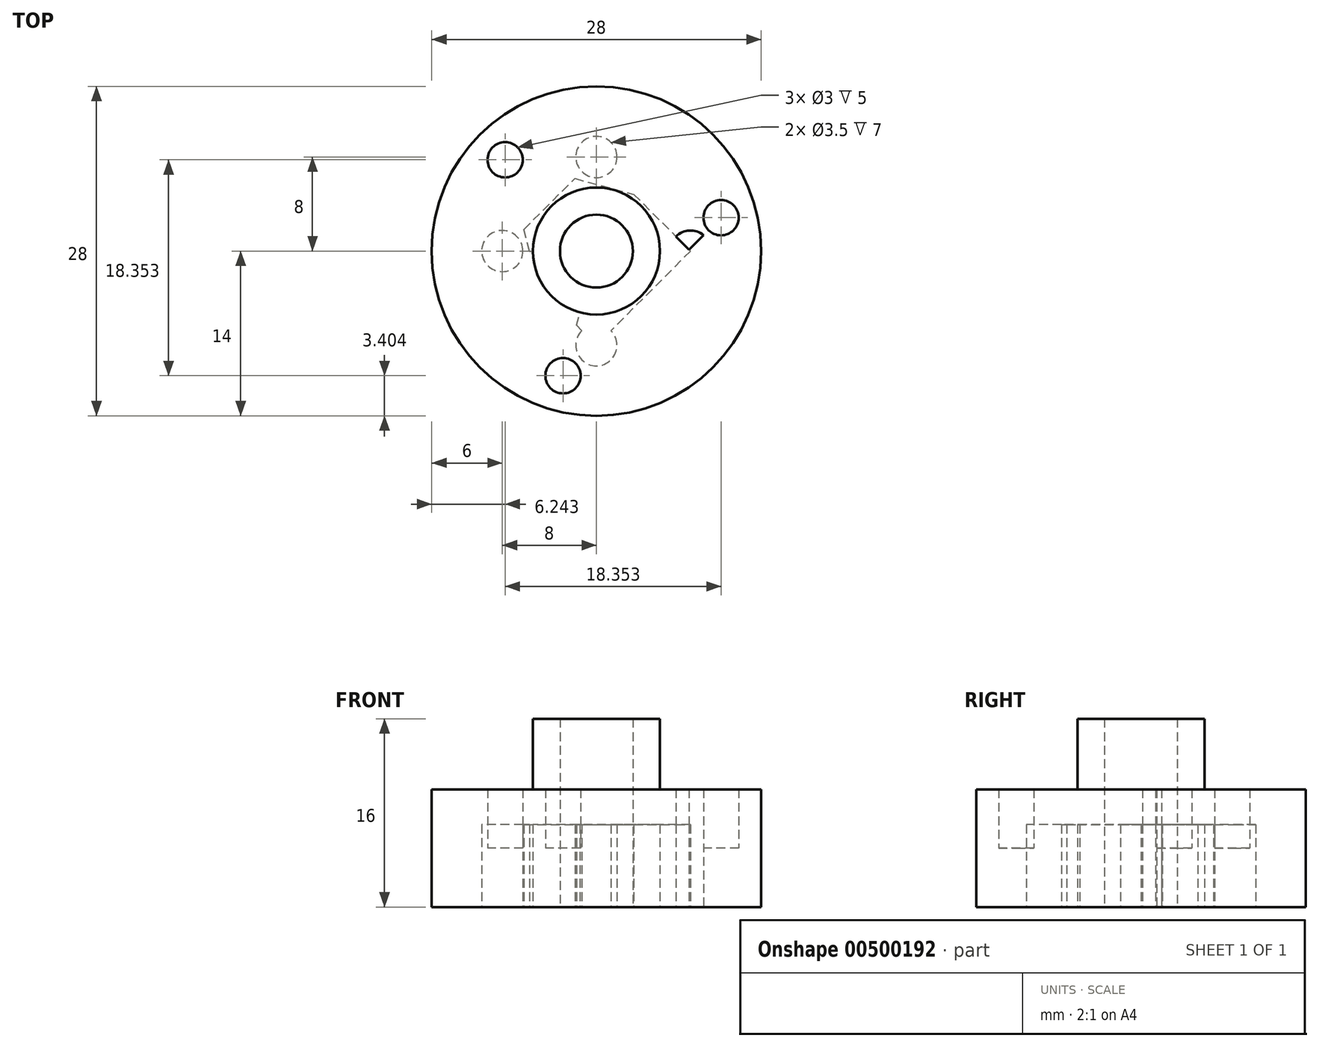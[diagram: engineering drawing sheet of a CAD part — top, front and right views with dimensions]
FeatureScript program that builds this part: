
annotation { "Feature Type Name" : "Feature", "Feature Type Description" : "" }
export const myFeature = defineFeature(function(context is Context, id is Id, definition is map)
    precondition{}
    {
        {
            var Q0;
            Q0=qCreatedBy(makeId("Top.planeOp"),FACE);
            var sketch = newSketch(context, id + "F0", { "sketchPlane" : qUnion([Q0])});
            skCircle(sketch, "E0", {"center": v(0, 0) * mm, "radius": 14 * mm});
            skCircle(sketch, "E1", {"center": v(0, 0) * mm, "radius": 3.1 * mm});
            skCircle(sketch, "E2", {"center": v(0, 0) * mm, "radius": 5.4 * mm});
            skLineSegment(sketch, "E3.0", {"start": v(-2.84, -10.6) * mm, "end": v(-7.76, 7.76) * mm});
            skLineSegment(sketch, "E3.1", {"start": v(-7.76, 7.76) * mm, "end": v(10.6, 2.84) * mm});
            skLineSegment(sketch, "E3.2", {"start": v(10.6, 2.84) * mm, "end": v(-2.84, -10.6) * mm});
            skLineSegment(sketch, "E4.0", {"start": v(8, 0) * mm, "end": v(0, -8) * mm});
            skLineSegment(sketch, "E4.1", {"start": v(0, -8) * mm, "end": v(-8, 0) * mm});
            skLineSegment(sketch, "E4.2", {"start": v(-8, 0) * mm, "end": v(0, 8) * mm});
            skLineSegment(sketch, "E4.3", {"start": v(0, 8) * mm, "end": v(8, 0) * mm});
            skPoint(sketch, "E5", {"position": v(-2.84, -10.6) * mm});
            skPoint(sketch, "E6", {"position": v(0, -8) * mm});
            skCircle(sketch, "E7", {"center": v(-8, 0) * mm, "radius": 1.75 * mm});
            skCircle(sketch, "E8", {"center": v(0, 8) * mm, "radius": 1.75 * mm});
            skCircle(sketch, "E9", {"center": v(8, 0) * mm, "radius": 1.75 * mm});
            skCircle(sketch, "E10", {"center": v(0, -8) * mm, "radius": 1.75 * mm});
            skLineSegment(sketch, "E11", {"start": v(-8, 0) * mm, "end": v(0, 0) * mm});
            skLineSegment(sketch, "E12", {"start": v(-2.84, -10.6) * mm, "end": v(0, 0) * mm});
            skCircle(sketch, "E13", {"center": v(-7.76, 7.76) * mm, "radius": 1.5 * mm});
            skCircle(sketch, "E14", {"center": v(-2.84, -10.6) * mm, "radius": 1.5 * mm});
            skCircle(sketch, "E15", {"center": v(10.6, 2.84) * mm, "radius": 1.5 * mm});
            skSolve(sketch);
        }
        {
            var Q0;
            Q0=makeQuery(id+"F0.imprint","IMPRINT",FACE,{"disambiguationData":[TD([[makeQuery(id+"F0.imprint","IMPRINT",EDGE,{"derivedFrom":sQuery(id+"F0.wireOp",EDGE,"E0")}),1.0]])]});
            var Q1;
            {var subQ5=sQuery(id+"F0.wireOp",EDGE,"E11");var subQ14=sQuery(id+"F0.wireOp",EDGE,"E2");var subQ15=makeQuery(id+"F0.imprint","INTERSECT",VERTEX,{"derivedFrom":[subQ14,subQ5]});Q1=makeQuery(id+"F0.imprint","IMPRINT",FACE,{"disambiguationData":[TD([[makeQuery(id+"F0.imprint","IMPRINT",EDGE,{"disambiguationData":[TD([[subQ15,1.0]])],"derivedFrom":subQ14}),-1.0]])]});}
            var Q2;
            {var subQ0=sQuery(id+"F0.wireOp",EDGE,"E9");var subQ1=sQuery(id+"F0.wireOp",EDGE,"E3.2");var subQ2=makeQuery(id+"F0.imprint","INTERSECT",VERTEX,{"disambiguationData":[OD(1.0)],"derivedFrom":[subQ1,subQ0]});Q2=makeQuery(id+"F0.imprint","IMPRINT",FACE,{"disambiguationData":[TD([[makeQuery(id+"F0.imprint","IMPRINT",EDGE,{"disambiguationData":[TD([[subQ2,-1.0]])],"derivedFrom":subQ1}),1.0]])]});}
            var Q3;
            {var subQ0=sQuery(id+"F0.wireOp",EDGE,"E4.3");var subQ1=sQuery(id+"F0.wireOp",EDGE,"E3.1");var subQ2=makeQuery(id+"F0.imprint","INTERSECT",VERTEX,{"derivedFrom":[subQ1,subQ0]});Q3=makeQuery(id+"F0.imprint","IMPRINT",FACE,{"disambiguationData":[TD([[makeQuery(id+"F0.imprint","IMPRINT",EDGE,{"disambiguationData":[TD([[subQ2,-1.0]])],"derivedFrom":subQ1}),-1.0]])]});}
            var Q4;
            {var subQ0=sQuery(id+"F0.wireOp",EDGE,"E4.2");var subQ1=sQuery(id+"F0.wireOp",EDGE,"E3.1");var subQ2=makeQuery(id+"F0.imprint","INTERSECT",VERTEX,{"derivedFrom":[subQ1,subQ0]});Q4=makeQuery(id+"F0.imprint","IMPRINT",FACE,{"disambiguationData":[TD([[makeQuery(id+"F0.imprint","IMPRINT",EDGE,{"disambiguationData":[TD([[subQ2,-1.0]])],"derivedFrom":subQ1}),1.0]])]});}
            var Q5;
            {var subQ0=sQuery(id+"F0.wireOp",EDGE,"E4.2");var subQ1=sQuery(id+"F0.wireOp",EDGE,"E3.0");var subQ2=makeQuery(id+"F0.imprint","INTERSECT",VERTEX,{"derivedFrom":[subQ1,subQ0]});Q5=makeQuery(id+"F0.imprint","IMPRINT",FACE,{"disambiguationData":[TD([[makeQuery(id+"F0.imprint","IMPRINT",EDGE,{"disambiguationData":[TD([[subQ2,-1.0]])],"derivedFrom":subQ1}),-1.0]])]});}
            var Q6;
            {var subQ0=sQuery(id+"F0.wireOp",EDGE,"E4.1");var subQ1=sQuery(id+"F0.wireOp",EDGE,"E3.0");var subQ2=makeQuery(id+"F0.imprint","INTERSECT",VERTEX,{"derivedFrom":[subQ1,subQ0]});Q6=makeQuery(id+"F0.imprint","IMPRINT",FACE,{"disambiguationData":[TD([[makeQuery(id+"F0.imprint","IMPRINT",EDGE,{"disambiguationData":[TD([[subQ2,-1.0]])],"derivedFrom":subQ1}),1.0]])]});}
            var Q7;
            {var subQ0=sQuery(id+"F0.wireOp",EDGE,"E11");var subQ1=sQuery(id+"F0.wireOp",EDGE,"E3.0");var subQ2=makeQuery(id+"F0.imprint","INTERSECT",VERTEX,{"derivedFrom":[subQ1,subQ0]});Q7=makeQuery(id+"F0.imprint","IMPRINT",FACE,{"disambiguationData":[TD([[makeQuery(id+"F0.imprint","IMPRINT",EDGE,{"disambiguationData":[TD([[subQ2,-1.0]])],"derivedFrom":subQ1}),1.0]])]});}
            var Q8;
            {var subQ0=sQuery(id+"F0.wireOp",EDGE,"E14");var subQ1=sQuery(id+"F0.wireOp",EDGE,"E3.0");var subQ2=makeQuery(id+"F0.imprint","INTERSECT",VERTEX,{"derivedFrom":[subQ1,subQ0]});Q8=makeQuery(id+"F0.imprint","IMPRINT",FACE,{"disambiguationData":[TD([[makeQuery(id+"F0.imprint","IMPRINT",EDGE,{"disambiguationData":[TD([[subQ2,-1.0]])],"derivedFrom":subQ1}),-1.0]])]});}
            var Q9;
            {var subQ0=sQuery(id+"F0.wireOp",EDGE,"E10");var subQ1=sQuery(id+"F0.wireOp",EDGE,"E3.2");var subQ2=makeQuery(id+"F0.imprint","INTERSECT",VERTEX,{"disambiguationData":[OD(1.0)],"derivedFrom":[subQ1,subQ0]});Q9=makeQuery(id+"F0.imprint","IMPRINT",FACE,{"disambiguationData":[TD([[makeQuery(id+"F0.imprint","IMPRINT",EDGE,{"disambiguationData":[TD([[subQ2,-1.0]])],"derivedFrom":subQ1}),-1.0]])]});}
            var Q10;
            {var subQ0=sQuery(id+"F0.wireOp",EDGE,"E11");var subQ1=sQuery(id+"F0.wireOp",EDGE,"E2");var subQ2=makeQuery(id+"F0.imprint","INTERSECT",VERTEX,{"derivedFrom":[subQ1,subQ0]});Q10=makeQuery(id+"F0.imprint","IMPRINT",FACE,{"disambiguationData":[TD([[makeQuery(id+"F0.imprint","IMPRINT",EDGE,{"disambiguationData":[TD([[subQ2,-1.0]])],"derivedFrom":subQ1}),-1.0]])]});}
            var Q11;
            {var subQ1=sQuery(id+"F0.wireOp",EDGE,"E4.2");var subQ3=sQuery(id+"F0.wireOp",EDGE,"E7");var subQ4=makeQuery(id+"F0.imprint","INTERSECT",VERTEX,{"derivedFrom":[subQ1,subQ3]});Q11=makeQuery(id+"F0.imprint","IMPRINT",FACE,{"disambiguationData":[TD([[makeQuery(id+"F0.imprint","IMPRINT",EDGE,{"disambiguationData":[TD([[subQ4,1.0]])],"derivedFrom":subQ3}),1.0]])]});}
            var Q12;
            {var subQ1=sQuery(id+"F0.wireOp",EDGE,"E4.1");var subQ3=sQuery(id+"F0.wireOp",EDGE,"E7");var subQ4=makeQuery(id+"F0.imprint","INTERSECT",VERTEX,{"derivedFrom":[subQ1,subQ3]});Q12=makeQuery(id+"F0.imprint","IMPRINT",FACE,{"disambiguationData":[TD([[makeQuery(id+"F0.imprint","IMPRINT",EDGE,{"disambiguationData":[TD([[subQ4,-1.0]])],"derivedFrom":subQ3}),1.0]])]});}
            var Q13;
            {var subQ1=sQuery(id+"F0.wireOp",EDGE,"E4.1");var subQ3=sQuery(id+"F0.wireOp",EDGE,"E7");var subQ4=makeQuery(id+"F0.imprint","INTERSECT",VERTEX,{"derivedFrom":[subQ1,subQ3]});Q13=makeQuery(id+"F0.imprint","IMPRINT",FACE,{"disambiguationData":[TD([[makeQuery(id+"F0.imprint","IMPRINT",EDGE,{"disambiguationData":[TD([[subQ4,1.0]])],"derivedFrom":subQ3}),1.0]])]});}
            var Q14;
            {var subQ0=sQuery(id+"F0.wireOp",EDGE,"E4.3");var subQ1=sQuery(id+"F0.wireOp",EDGE,"E4.2");var subQ2=makeQuery(id+"F0.imprint","INTERSECT",VERTEX,{"derivedFrom":[subQ1,subQ0]});Q14=makeQuery(id+"F0.imprint","IMPRINT",FACE,{"disambiguationData":[TD([[makeQuery(id+"F0.imprint","IMPRINT",EDGE,{"disambiguationData":[TD([[subQ2,1.0]])],"derivedFrom":subQ1}),1.0]])]});}
            var Q15;
            {var subQ0=sQuery(id+"F0.wireOp",EDGE,"E4.3");var subQ1=sQuery(id+"F0.wireOp",EDGE,"E4.2");var subQ2=makeQuery(id+"F0.imprint","INTERSECT",VERTEX,{"derivedFrom":[subQ1,subQ0]});Q15=makeQuery(id+"F0.imprint","IMPRINT",FACE,{"disambiguationData":[TD([[makeQuery(id+"F0.imprint","IMPRINT",EDGE,{"disambiguationData":[TD([[subQ2,1.0]])],"derivedFrom":subQ1}),-1.0]])]});}
            var Q16;
            {var subQ0=sQuery(id+"F0.wireOp",EDGE,"E9");var subQ1=sQuery(id+"F0.wireOp",EDGE,"E3.2");var subQ2=makeQuery(id+"F0.imprint","INTERSECT",VERTEX,{"disambiguationData":[OD(0.0)],"derivedFrom":[subQ1,subQ0]});Q16=makeQuery(id+"F0.imprint","IMPRINT",FACE,{"disambiguationData":[TD([[makeQuery(id+"F0.imprint","IMPRINT",EDGE,{"disambiguationData":[TD([[subQ2,-1.0]])],"derivedFrom":subQ1}),1.0]])]});}
            var Q17;
            {var subQ0=sQuery(id+"F0.wireOp",EDGE,"E4.3");var subQ1=sQuery(id+"F0.wireOp",EDGE,"E3.2");var subQ2=makeQuery(id+"F0.imprint","INTERSECT",VERTEX,{"derivedFrom":[subQ1,subQ0]});Q17=makeQuery(id+"F0.imprint","IMPRINT",FACE,{"disambiguationData":[TD([[makeQuery(id+"F0.imprint","IMPRINT",EDGE,{"disambiguationData":[TD([[subQ2,-1.0]])],"derivedFrom":subQ1}),-1.0]])]});}
            var Q18;
            {var subQ0=sQuery(id+"F0.wireOp",EDGE,"E4.1");var subQ1=sQuery(id+"F0.wireOp",EDGE,"E3.2");var subQ2=makeQuery(id+"F0.imprint","INTERSECT",VERTEX,{"derivedFrom":[subQ1,subQ0]});Q18=makeQuery(id+"F0.imprint","IMPRINT",FACE,{"disambiguationData":[TD([[makeQuery(id+"F0.imprint","IMPRINT",EDGE,{"disambiguationData":[TD([[subQ2,-1.0]])],"derivedFrom":subQ1}),1.0]])]});}
            var Q19;
            {var subQ0=sQuery(id+"F0.wireOp",EDGE,"E10");var subQ1=sQuery(id+"F0.wireOp",EDGE,"E3.2");var subQ2=makeQuery(id+"F0.imprint","INTERSECT",VERTEX,{"disambiguationData":[OD(0.0)],"derivedFrom":[subQ1,subQ0]});Q19=makeQuery(id+"F0.imprint","IMPRINT",FACE,{"disambiguationData":[TD([[makeQuery(id+"F0.imprint","IMPRINT",EDGE,{"disambiguationData":[TD([[subQ2,-1.0]])],"derivedFrom":subQ1}),-1.0]])]});}
            var Q20;
            {var subQ0=sQuery(id+"F0.wireOp",EDGE,"E4.1");var subQ1=sQuery(id+"F0.wireOp",EDGE,"E3.2");var subQ2=makeQuery(id+"F0.imprint","INTERSECT",VERTEX,{"derivedFrom":[subQ1,subQ0]});Q20=makeQuery(id+"F0.imprint","IMPRINT",FACE,{"disambiguationData":[TD([[makeQuery(id+"F0.imprint","IMPRINT",EDGE,{"disambiguationData":[TD([[subQ2,-1.0]])],"derivedFrom":subQ1}),-1.0]])]});}
            var Q21;
            {var subQ0=sQuery(id+"F0.wireOp",EDGE,"E10");var subQ1=sQuery(id+"F0.wireOp",EDGE,"E3.2");var subQ2=makeQuery(id+"F0.imprint","INTERSECT",VERTEX,{"disambiguationData":[OD(0.0)],"derivedFrom":[subQ1,subQ0]});Q21=makeQuery(id+"F0.imprint","IMPRINT",FACE,{"disambiguationData":[TD([[makeQuery(id+"F0.imprint","IMPRINT",EDGE,{"disambiguationData":[TD([[subQ2,-1.0]])],"derivedFrom":subQ1}),1.0]])]});}
            var Q22;
            {var subQ0=sQuery(id+"F0.wireOp",EDGE,"E9");var subQ1=sQuery(id+"F0.wireOp",EDGE,"E3.2");var subQ2=makeQuery(id+"F0.imprint","INTERSECT",VERTEX,{"disambiguationData":[OD(0.0)],"derivedFrom":[subQ1,subQ0]});Q22=makeQuery(id+"F0.imprint","IMPRINT",FACE,{"disambiguationData":[TD([[makeQuery(id+"F0.imprint","IMPRINT",EDGE,{"disambiguationData":[TD([[subQ2,-1.0]])],"derivedFrom":subQ1}),-1.0]])]});}
            var Q23;
            {var subQ0=sQuery(id+"F0.wireOp",EDGE,"E4.3");var subQ1=sQuery(id+"F0.wireOp",EDGE,"E3.2");var subQ2=makeQuery(id+"F0.imprint","INTERSECT",VERTEX,{"derivedFrom":[subQ1,subQ0]});Q23=makeQuery(id+"F0.imprint","IMPRINT",FACE,{"disambiguationData":[TD([[makeQuery(id+"F0.imprint","IMPRINT",EDGE,{"disambiguationData":[TD([[subQ2,-1.0]])],"derivedFrom":subQ1}),1.0]])]});}
            extrude(context, id + "F1", {"entities" : qUnion([Q0, Q1, Q2, Q3, Q4, Q5, Q6, Q7, Q8, Q9, Q10, Q11, Q12, Q13, Q14, Q15, Q16, Q17, Q18, Q19, Q20, Q21, Q22, Q23]), "depth" : 10 * mm});
        }
        {
            var Q0;
            {var subQ0=sQuery(id+"F0.wireOp",EDGE,"E11");var subQ1=sQuery(id+"F0.wireOp",EDGE,"E1");var subQ2=makeQuery(id+"F0.imprint","INTERSECT",VERTEX,{"derivedFrom":[subQ1,subQ0]});Q0=makeQuery(id+"F0.imprint","IMPRINT",FACE,{"disambiguationData":[TD([[makeQuery(id+"F0.imprint","IMPRINT",EDGE,{"disambiguationData":[TD([[subQ2,-1.0]])],"derivedFrom":subQ1}),-1.0]])]});}
            var Q1;
            {var subQ0=sQuery(id+"F0.wireOp",EDGE,"E11");var subQ1=sQuery(id+"F0.wireOp",EDGE,"E1");var subQ2=makeQuery(id+"F0.imprint","INTERSECT",VERTEX,{"derivedFrom":[subQ1,subQ0]});Q1=makeQuery(id+"F0.imprint","IMPRINT",FACE,{"disambiguationData":[TD([[makeQuery(id+"F0.imprint","IMPRINT",EDGE,{"disambiguationData":[TD([[subQ2,1.0]])],"derivedFrom":subQ1}),-1.0]])]});}
            extrude(context, id + "F2", {"entities" : qUnion([Q0, Q1]), "operationType" : NewBodyOperationType.ADD, "depth" : 16 * mm});
        }
        {
            var Q0;
            {var subQ1=sQuery(id+"F0.wireOp",EDGE,"E3.2");var subQ3=sQuery(id+"F0.wireOp",EDGE,"E14");var subQ4=makeQuery(id+"F0.imprint","INTERSECT",VERTEX,{"derivedFrom":[subQ1,subQ3]});Q0=makeQuery(id+"F0.imprint","IMPRINT",FACE,{"disambiguationData":[TD([[makeQuery(id+"F0.imprint","IMPRINT",EDGE,{"disambiguationData":[TD([[subQ4,-1.0]])],"derivedFrom":subQ3}),1.0]])]});}
            var Q1;
            {var subQ1=sQuery(id+"F0.wireOp",EDGE,"E3.0");var subQ3=sQuery(id+"F0.wireOp",EDGE,"E14");var subQ4=makeQuery(id+"F0.imprint","INTERSECT",VERTEX,{"derivedFrom":[subQ1,subQ3]});Q1=makeQuery(id+"F0.imprint","IMPRINT",FACE,{"disambiguationData":[TD([[makeQuery(id+"F0.imprint","IMPRINT",EDGE,{"disambiguationData":[TD([[subQ4,1.0]])],"derivedFrom":subQ3}),1.0]])]});}
            var Q2;
            {var subQ1=sQuery(id+"F0.wireOp",EDGE,"E3.0");var subQ3=sQuery(id+"F0.wireOp",EDGE,"E14");var subQ4=makeQuery(id+"F0.imprint","INTERSECT",VERTEX,{"derivedFrom":[subQ1,subQ3]});Q2=makeQuery(id+"F0.imprint","IMPRINT",FACE,{"disambiguationData":[TD([[makeQuery(id+"F0.imprint","IMPRINT",EDGE,{"disambiguationData":[TD([[subQ4,-1.0]])],"derivedFrom":subQ3}),1.0]])]});}
            var Q3;
            {var subQ0=sQuery(id+"F0.wireOp",EDGE,"E3.2");var subQ1=sQuery(id+"F0.wireOp",EDGE,"E3.1");var subQ2=makeQuery(id+"F0.imprint","INTERSECT",VERTEX,{"derivedFrom":[subQ1,subQ0]});Q3=makeQuery(id+"F0.imprint","IMPRINT",FACE,{"disambiguationData":[TD([[makeQuery(id+"F0.imprint","IMPRINT",EDGE,{"disambiguationData":[TD([[subQ2,1.0]])],"derivedFrom":subQ1}),-1.0]])]});}
            var Q4;
            {var subQ0=sQuery(id+"F0.wireOp",EDGE,"E3.2");var subQ1=sQuery(id+"F0.wireOp",EDGE,"E3.1");var subQ2=makeQuery(id+"F0.imprint","INTERSECT",VERTEX,{"derivedFrom":[subQ1,subQ0]});Q4=makeQuery(id+"F0.imprint","IMPRINT",FACE,{"disambiguationData":[TD([[makeQuery(id+"F0.imprint","IMPRINT",EDGE,{"disambiguationData":[TD([[subQ2,1.0]])],"derivedFrom":subQ1}),1.0]])]});}
            var Q5;
            {var subQ0=sQuery(id+"F0.wireOp",EDGE,"E3.1");var subQ1=sQuery(id+"F0.wireOp",EDGE,"E3.0");var subQ2=makeQuery(id+"F0.imprint","INTERSECT",VERTEX,{"derivedFrom":[subQ1,subQ0]});Q5=makeQuery(id+"F0.imprint","IMPRINT",FACE,{"disambiguationData":[TD([[makeQuery(id+"F0.imprint","IMPRINT",EDGE,{"disambiguationData":[TD([[subQ2,1.0]])],"derivedFrom":subQ1}),1.0]])]});}
            var Q6;
            {var subQ0=sQuery(id+"F0.wireOp",EDGE,"E3.1");var subQ1=sQuery(id+"F0.wireOp",EDGE,"E3.0");var subQ2=makeQuery(id+"F0.imprint","INTERSECT",VERTEX,{"derivedFrom":[subQ1,subQ0]});Q6=makeQuery(id+"F0.imprint","IMPRINT",FACE,{"disambiguationData":[TD([[makeQuery(id+"F0.imprint","IMPRINT",EDGE,{"disambiguationData":[TD([[subQ2,1.0]])],"derivedFrom":subQ1}),-1.0]])]});}
            extrude(context, id + "F3", {"entities" : qUnion([Q0, Q1, Q2, Q3, Q4, Q5, Q6]), "operationType" : NewBodyOperationType.ADD, "depth" : 5 * mm});
        }
        {
            var Q0;
            {var subQ0=sQuery(id+"F0.wireOp",EDGE,"E4.3");var subQ1=sQuery(id+"F0.wireOp",EDGE,"E4.2");var subQ2=makeQuery(id+"F0.imprint","INTERSECT",VERTEX,{"derivedFrom":[subQ1,subQ0]});Q0=makeQuery(id+"F0.imprint","IMPRINT",FACE,{"disambiguationData":[TD([[makeQuery(id+"F0.imprint","IMPRINT",EDGE,{"disambiguationData":[TD([[subQ2,1.0]])],"derivedFrom":subQ1}),1.0]])]});}
            var Q1;
            {var subQ0=sQuery(id+"F0.wireOp",EDGE,"E4.3");var subQ1=sQuery(id+"F0.wireOp",EDGE,"E4.2");var subQ2=makeQuery(id+"F0.imprint","INTERSECT",VERTEX,{"derivedFrom":[subQ1,subQ0]});Q1=makeQuery(id+"F0.imprint","IMPRINT",FACE,{"disambiguationData":[TD([[makeQuery(id+"F0.imprint","IMPRINT",EDGE,{"disambiguationData":[TD([[subQ2,1.0]])],"derivedFrom":subQ1}),-1.0]])]});}
            var Q2;
            {var subQ1=sQuery(id+"F0.wireOp",EDGE,"E4.1");var subQ3=sQuery(id+"F0.wireOp",EDGE,"E7");var subQ4=makeQuery(id+"F0.imprint","INTERSECT",VERTEX,{"derivedFrom":[subQ1,subQ3]});Q2=makeQuery(id+"F0.imprint","IMPRINT",FACE,{"disambiguationData":[TD([[makeQuery(id+"F0.imprint","IMPRINT",EDGE,{"disambiguationData":[TD([[subQ4,1.0]])],"derivedFrom":subQ3}),1.0]])]});}
            var Q3;
            {var subQ1=sQuery(id+"F0.wireOp",EDGE,"E4.1");var subQ3=sQuery(id+"F0.wireOp",EDGE,"E7");var subQ4=makeQuery(id+"F0.imprint","INTERSECT",VERTEX,{"derivedFrom":[subQ1,subQ3]});Q3=makeQuery(id+"F0.imprint","IMPRINT",FACE,{"disambiguationData":[TD([[makeQuery(id+"F0.imprint","IMPRINT",EDGE,{"disambiguationData":[TD([[subQ4,-1.0]])],"derivedFrom":subQ3}),1.0]])]});}
            var Q4;
            {var subQ1=sQuery(id+"F0.wireOp",EDGE,"E4.2");var subQ3=sQuery(id+"F0.wireOp",EDGE,"E7");var subQ4=makeQuery(id+"F0.imprint","INTERSECT",VERTEX,{"derivedFrom":[subQ1,subQ3]});Q4=makeQuery(id+"F0.imprint","IMPRINT",FACE,{"disambiguationData":[TD([[makeQuery(id+"F0.imprint","IMPRINT",EDGE,{"disambiguationData":[TD([[subQ4,1.0]])],"derivedFrom":subQ3}),1.0]])]});}
            var Q5;
            {var subQ0=sQuery(id+"F0.wireOp",EDGE,"E10");var subQ1=sQuery(id+"F0.wireOp",EDGE,"E3.2");var subQ2=makeQuery(id+"F0.imprint","INTERSECT",VERTEX,{"disambiguationData":[OD(0.0)],"derivedFrom":[subQ1,subQ0]});Q5=makeQuery(id+"F0.imprint","IMPRINT",FACE,{"disambiguationData":[TD([[makeQuery(id+"F0.imprint","IMPRINT",EDGE,{"disambiguationData":[TD([[subQ2,-1.0]])],"derivedFrom":subQ1}),-1.0]])]});}
            var Q6;
            {var subQ0=sQuery(id+"F0.wireOp",EDGE,"E4.1");var subQ1=sQuery(id+"F0.wireOp",EDGE,"E3.2");var subQ2=makeQuery(id+"F0.imprint","INTERSECT",VERTEX,{"derivedFrom":[subQ1,subQ0]});Q6=makeQuery(id+"F0.imprint","IMPRINT",FACE,{"disambiguationData":[TD([[makeQuery(id+"F0.imprint","IMPRINT",EDGE,{"disambiguationData":[TD([[subQ2,-1.0]])],"derivedFrom":subQ1}),-1.0]])]});}
            var Q7;
            {var subQ0=sQuery(id+"F0.wireOp",EDGE,"E10");var subQ1=sQuery(id+"F0.wireOp",EDGE,"E3.2");var subQ2=makeQuery(id+"F0.imprint","INTERSECT",VERTEX,{"disambiguationData":[OD(0.0)],"derivedFrom":[subQ1,subQ0]});Q7=makeQuery(id+"F0.imprint","IMPRINT",FACE,{"disambiguationData":[TD([[makeQuery(id+"F0.imprint","IMPRINT",EDGE,{"disambiguationData":[TD([[subQ2,-1.0]])],"derivedFrom":subQ1}),1.0]])]});}
            var Q8;
            {var subQ0=sQuery(id+"F0.wireOp",EDGE,"E4.1");var subQ1=sQuery(id+"F0.wireOp",EDGE,"E3.2");var subQ2=makeQuery(id+"F0.imprint","INTERSECT",VERTEX,{"derivedFrom":[subQ1,subQ0]});Q8=makeQuery(id+"F0.imprint","IMPRINT",FACE,{"disambiguationData":[TD([[makeQuery(id+"F0.imprint","IMPRINT",EDGE,{"disambiguationData":[TD([[subQ2,-1.0]])],"derivedFrom":subQ1}),1.0]])]});}
            var Q9;
            {var subQ0=sQuery(id+"F0.wireOp",EDGE,"E9");var subQ1=sQuery(id+"F0.wireOp",EDGE,"E3.2");var subQ2=makeQuery(id+"F0.imprint","INTERSECT",VERTEX,{"disambiguationData":[OD(0.0)],"derivedFrom":[subQ1,subQ0]});Q9=makeQuery(id+"F0.imprint","IMPRINT",FACE,{"disambiguationData":[TD([[makeQuery(id+"F0.imprint","IMPRINT",EDGE,{"disambiguationData":[TD([[subQ2,-1.0]])],"derivedFrom":subQ1}),-1.0]])]});}
            var Q10;
            {var subQ0=sQuery(id+"F0.wireOp",EDGE,"E4.3");var subQ1=sQuery(id+"F0.wireOp",EDGE,"E3.2");var subQ2=makeQuery(id+"F0.imprint","INTERSECT",VERTEX,{"derivedFrom":[subQ1,subQ0]});Q10=makeQuery(id+"F0.imprint","IMPRINT",FACE,{"disambiguationData":[TD([[makeQuery(id+"F0.imprint","IMPRINT",EDGE,{"disambiguationData":[TD([[subQ2,-1.0]])],"derivedFrom":subQ1}),-1.0]])]});}
            var Q11;
            {var subQ0=sQuery(id+"F0.wireOp",EDGE,"E9");var subQ1=sQuery(id+"F0.wireOp",EDGE,"E3.2");var subQ2=makeQuery(id+"F0.imprint","INTERSECT",VERTEX,{"disambiguationData":[OD(0.0)],"derivedFrom":[subQ1,subQ0]});Q11=makeQuery(id+"F0.imprint","IMPRINT",FACE,{"disambiguationData":[TD([[makeQuery(id+"F0.imprint","IMPRINT",EDGE,{"disambiguationData":[TD([[subQ2,-1.0]])],"derivedFrom":subQ1}),1.0]])]});}
            var Q12;
            {var subQ0=sQuery(id+"F0.wireOp",EDGE,"E9");var subQ1=sQuery(id+"F0.wireOp",EDGE,"E3.2");var subQ2=makeQuery(id+"F0.imprint","INTERSECT",VERTEX,{"disambiguationData":[OD(0.0)],"derivedFrom":[subQ1,subQ0]});Q12=makeQuery(id+"F0.imprint","IMPRINT",FACE,{"disambiguationData":[TD([[makeQuery(id+"F0.imprint","IMPRINT",EDGE,{"disambiguationData":[TD([[subQ2,-1.0]])],"derivedFrom":subQ1}),1.0]])]});}
            var Q13;
            {var subQ0=sQuery(id+"F0.wireOp",EDGE,"E4.3");var subQ1=sQuery(id+"F0.wireOp",EDGE,"E3.2");var subQ2=makeQuery(id+"F0.imprint","INTERSECT",VERTEX,{"derivedFrom":[subQ1,subQ0]});Q13=makeQuery(id+"F0.imprint","IMPRINT",FACE,{"disambiguationData":[TD([[makeQuery(id+"F0.imprint","IMPRINT",EDGE,{"disambiguationData":[TD([[subQ2,-1.0]])],"derivedFrom":subQ1}),1.0]])]});}
            extrude(context, id + "F4", {"entities" : qUnion([Q0, Q1, Q2, Q3, Q4, Q5, Q6, Q7, Q8, Q9, Q10, Q11, Q12, Q13]), "operationType" : NewBodyOperationType.REMOVE, "depth" : 7 * mm});
        }
    });
